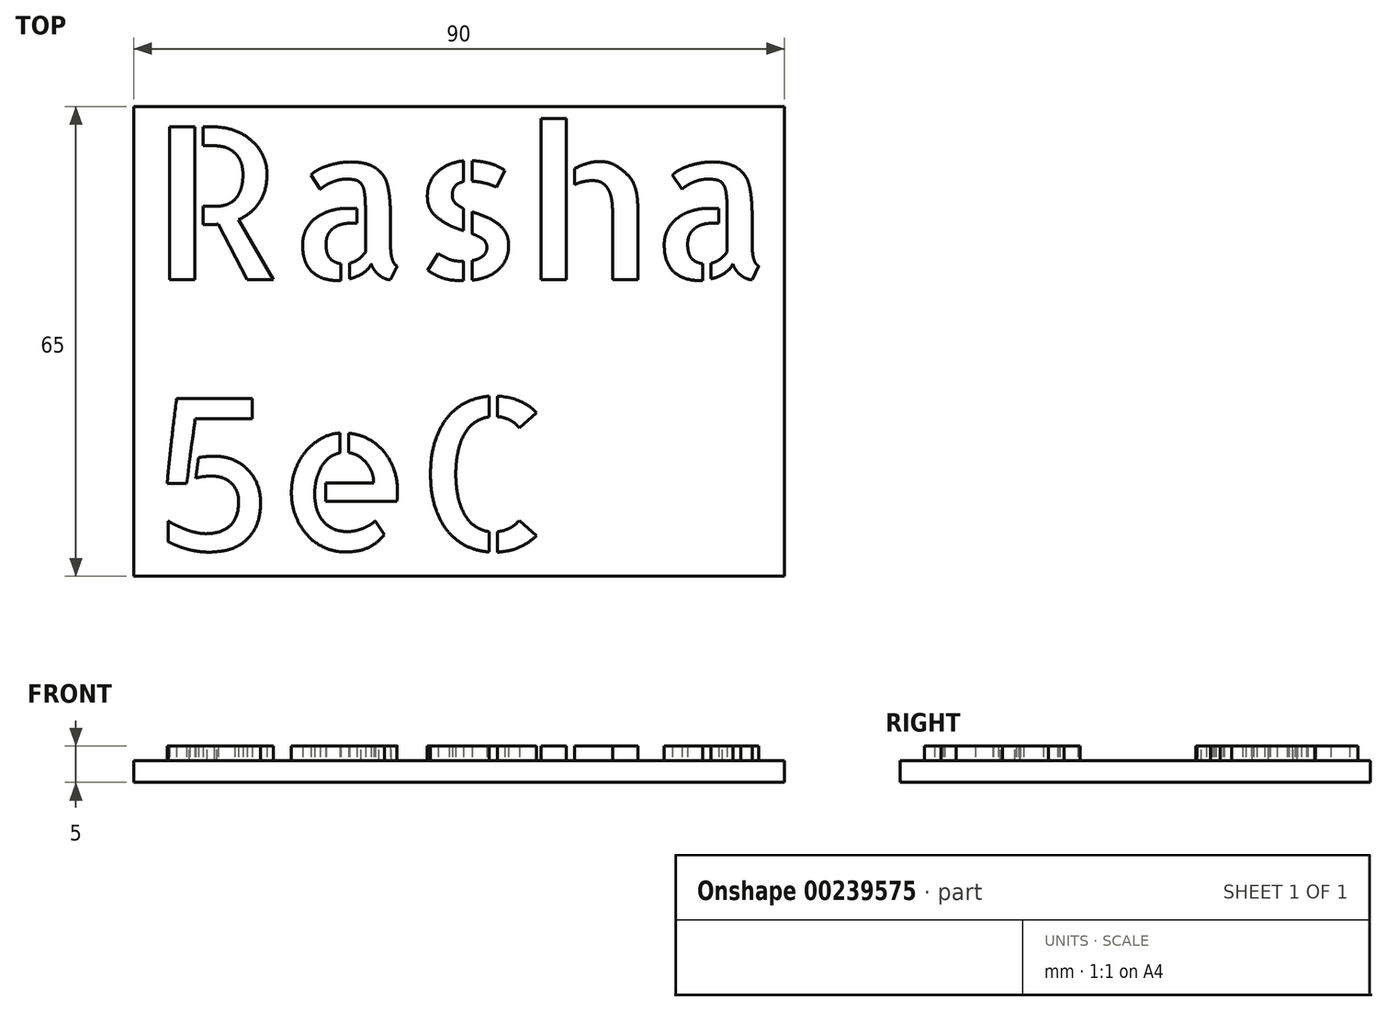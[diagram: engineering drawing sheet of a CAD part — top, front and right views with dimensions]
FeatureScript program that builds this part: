
annotation { "Feature Type Name" : "Feature", "Feature Type Description" : "" }
export const myFeature = defineFeature(function(context is Context, id is Id, definition is map)
    precondition{}
    {
        {
            var Q0;
            Q0=qCreatedBy(makeId("Top.planeOp"),FACE);
            var sketch = newSketch(context, id + "F0", { "sketchPlane" : qUnion([Q0])});
            skLineSegment(sketch, "E0.bottom", {"start": v(0, 0) * mm, "end": v(90, 0) * mm});
            skLineSegment(sketch, "E0.top", {"start": v(0, -65) * mm, "end": v(90, -65) * mm});
            skLineSegment(sketch, "E0.left", {"start": v(0, 0) * mm, "end": v(0, -65) * mm});
            skLineSegment(sketch, "E0.right", {"start": v(90, 0) * mm, "end": v(90, -65) * mm});
            skSolve(sketch);
        }
        {
            var Q0;
            Q0=makeQuery(id+"F0.imprint","IMPRINT",FACE,{"disambiguationData":[TD([[makeQuery(id+"F0.imprint","IMPRINT",EDGE,{"derivedFrom":sQuery(id+"F0.wireOp",EDGE,"E0.bottom")}),-1.0]])]});
            extrude(context, id + "F1", {"entities" : qUnion([Q0]), "depth" : 3 * mm});
        }
        {
            var Q0;
            Q0=makeQuery(id+"F1.opExtrude","CAP_FACE",FACE,{"disambiguationData":[OSD([sQuery(id+"F0.wireOp",EDGE,"E0.bottom"),sQuery(id+"F0.wireOp",EDGE,"E0.top"),sQuery(id+"F0.wireOp",EDGE,"E0.left"),sQuery(id+"F0.wireOp",EDGE,"E0.right")])],"isStart":false});
            var sketch = newSketch(context, id + "F2", { "sketchPlane" : qUnion([Q0])});
            skText(sketch, "E1", { "text": "Rasha\n5eC", "fontName": "AllertaStencil-Regular.ttf"});
            const initialGuessF2  = {"E1": [0.00242, -0.02395, 1, 0, 0.02113]};
            skSetInitialGuess(sketch, initialGuessF2);
            skSolve(sketch);
        }
        {
            var Q0;
            Q0 = qSketchRegion(id + "F2", true);
            extrude(context, id + "F3", {"entities" : qUnion([Q0]), "operationType" : NewBodyOperationType.ADD, "depth" : 2 * mm});
        }
    });
